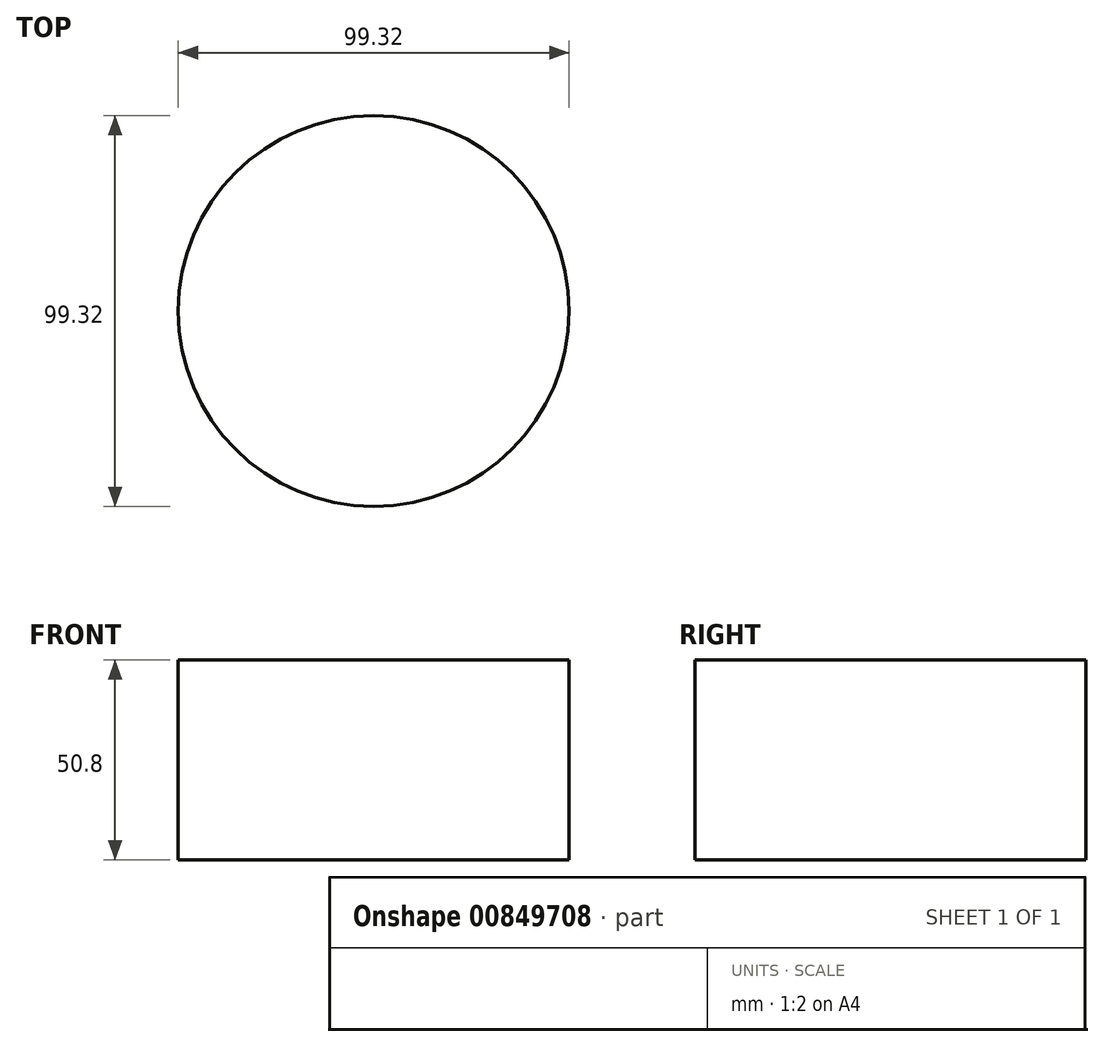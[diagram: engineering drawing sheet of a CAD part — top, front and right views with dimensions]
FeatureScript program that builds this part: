
annotation { "Feature Type Name" : "Feature", "Feature Type Description" : "" }
export const myFeature = defineFeature(function(context is Context, id is Id, definition is map)
    precondition{}
    {
        {
            var Q0;
            Q0=qCreatedBy(makeId("Top.planeOp"),FACE);
            var sketch = newSketch(context, id + "F0", { "sketchPlane" : qUnion([Q0])});
            skCircle(sketch, "E0", {"center": v(0, 0) * mm, "radius": 49.66 * mm});
            skLineSegment(sketch, "E1", {"start": v(0, 0) * mm, "end": v(0, 0) * mm});
            skSolve(sketch);
        }
        {
            var Q0;
            Q0 = qSketchRegion(id + "F0", true);
            extrude(context, id + "F1", {"entities" : qUnion([Q0]), "depth" : 50.8 * mm, "offsetDistance" : 25.4 * mm});
        }
    });
